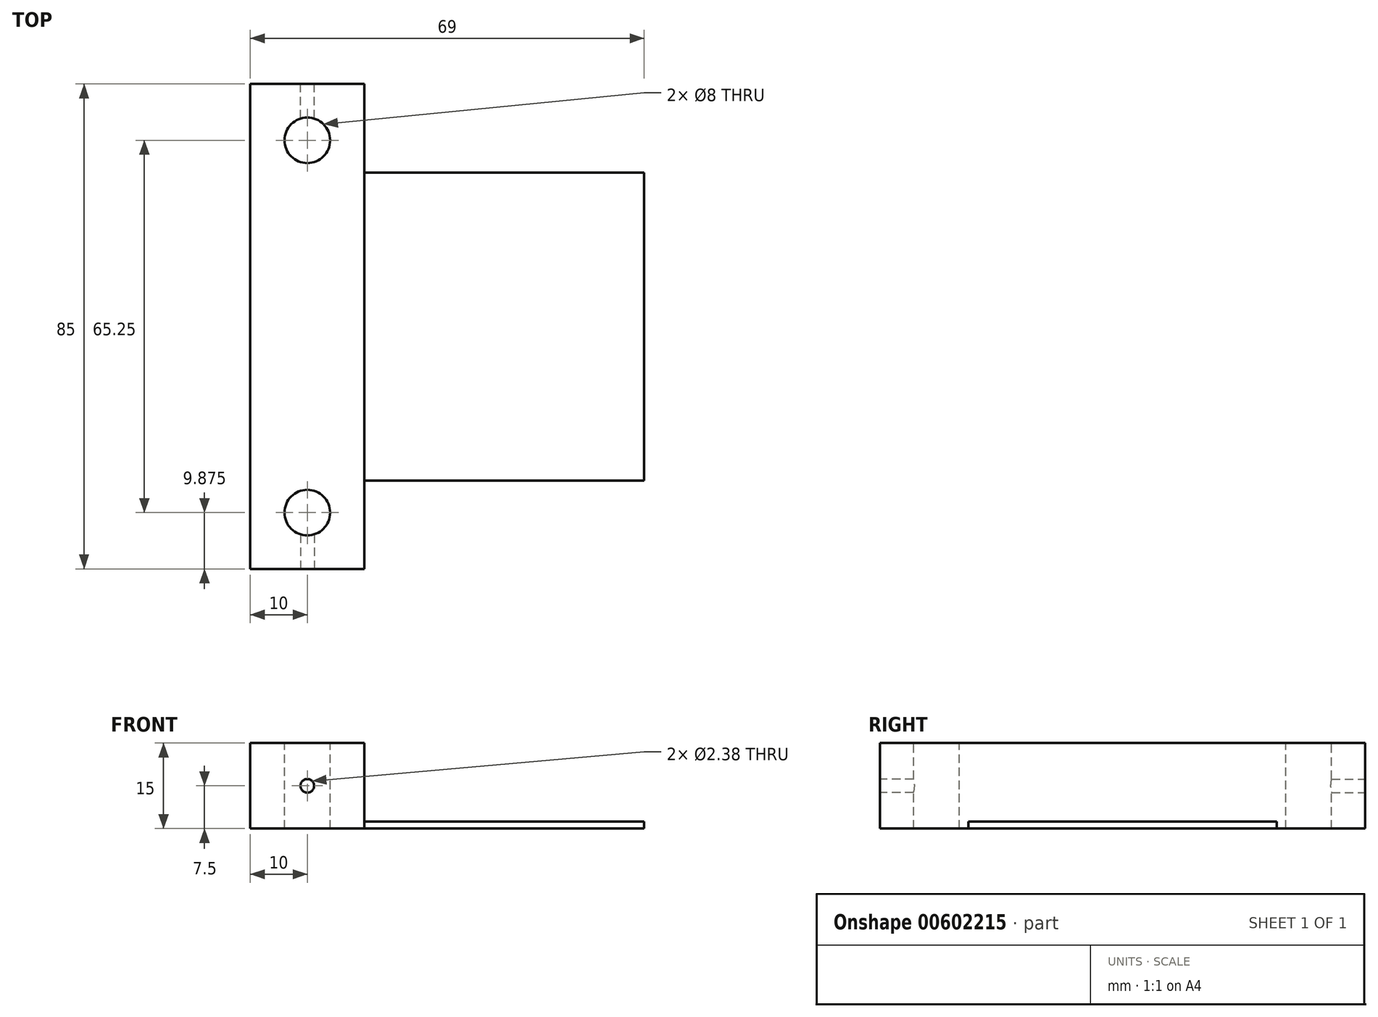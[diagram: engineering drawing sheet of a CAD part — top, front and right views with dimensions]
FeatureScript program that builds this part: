
annotation { "Feature Type Name" : "Feature", "Feature Type Description" : "" }
export const myFeature = defineFeature(function(context is Context, id is Id, definition is map)
    precondition{}
    {
        {
            var Q0;
            Q0=qCreatedBy(makeId("Front.planeOp"),FACE);
            var sketch = newSketch(context, id + "F0", { "sketchPlane" : qUnion([Q0])});
            skLineSegment(sketch, "E0.bottom", {"start": v(0, 0) * mm, "end": v(20, 0) * mm});
            skLineSegment(sketch, "E0.top", {"start": v(0, 15) * mm, "end": v(20, 15) * mm});
            skLineSegment(sketch, "E0.left", {"start": v(0, 0) * mm, "end": v(0, 15) * mm});
            skLineSegment(sketch, "E0.right", {"start": v(20, 0) * mm, "end": v(20, 15) * mm});
            skLineSegment(sketch, "E1", {"start": v(69, 1.2) * mm, "end": v(69, 0) * mm});
            skLineSegment(sketch, "E2", {"start": v(69, 0) * mm, "end": v(20, 0) * mm});
            skLineSegment(sketch, "E3", {"start": v(69, 1.2) * mm, "end": v(20, 1.2) * mm});
            skSolve(sketch);
        }
        {
            var Q0;
            Q0=makeQuery(id+"F0.imprint","IMPRINT",FACE,{"disambiguationData":[TD([[makeQuery(id+"F0.imprint","IMPRINT",EDGE,{"derivedFrom":sQuery(id+"F0.wireOp",EDGE,"E0.right")}),-1.0]])]});
            extrude(context, id + "F1", {"entities" : qUnion([Q0]), "endBound" : BoundingType.SYMMETRIC, "oppositeDirection" : true, "depth" : 53.98 * mm, "offsetDistance" : 25 * mm});
        }
        {
            var Q0;
            Q0=makeQuery(id+"F0.imprint","IMPRINT",FACE,{"disambiguationData":[TD([[makeQuery(id+"F0.imprint","IMPRINT",EDGE,{"derivedFrom":sQuery(id+"F0.wireOp",EDGE,"E0.bottom")}),1.0]])]});
            extrude(context, id + "F2", {"entities" : qUnion([Q0]), "operationType" : NewBodyOperationType.ADD, "endBound" : BoundingType.SYMMETRIC, "depth" : 85 * mm, "offsetDistance" : 25 * mm});
        }
        {
            var Q0;
            Q0=makeQuery(id+"F2.opExtrude","SWEPT_FACE",FACE,{"disambiguationData":[OSD([sQuery(id+"F0.wireOp",EDGE,"E0.top")])]});
            cPlane(context, id + "F3", {"entities" : qUnion([Q0]), "cplaneType" : CPlaneType.OFFSET, "offset" : 0 * mm, "width" : 150 * mm, "height" : 150 * mm});
        }
        {
            var Q0;
            Q0=qCreatedBy(id+"F3.planeOp",FACE);
            var sketch = newSketch(context, id + "F4", { "sketchPlane" : qUnion([Q0])});
            skLineSegment(sketch, "E4.0", {"start": v(0, -42.5) * mm, "end": v(0, 42.5) * mm});
            skLineSegment(sketch, "E4.1", {"start": v(0, -42.5) * mm, "end": v(20, -42.5) * mm});
            skLineSegment(sketch, "E4.2", {"start": v(20, -42.5) * mm, "end": v(20, -42.5) * mm});
            skLineSegment(sketch, "E4.3", {"start": v(20, 42.5) * mm, "end": v(20, 42.5) * mm});
            skLineSegment(sketch, "E4.4", {"start": v(0, 42.5) * mm, "end": v(20, 42.5) * mm});
            skCircle(sketch, "E5", {"center": v(10, -32.62) * mm, "radius": 4 * mm});
            skLineSegment(sketch, "E6", {"start": v(20, -32.62) * mm, "end": v(0, -32.62) * mm, "construction": true});
            skLineSegment(sketch, "E7", {"start": v(20, -36.62) * mm, "end": v(0, -36.62) * mm, "construction": true});
            skCircle(sketch, "E8", {"center": v(10, 32.62) * mm, "radius": 4 * mm});
            skLineSegment(sketch, "E9", {"start": v(20, 32.62) * mm, "end": v(0, 32.62) * mm, "construction": true});
            skLineSegment(sketch, "E10", {"start": v(0, 36.62) * mm, "end": v(20, 36.62) * mm, "construction": true});
            skLineSegment(sketch, "E11", {"start": v(20, -42.5) * mm, "end": v(20, -36.62) * mm, "construction": true});
            skLineSegment(sketch, "E12", {"start": v(20, 36.62) * mm, "end": v(20, 42.5) * mm, "construction": true});
            skSolve(sketch);
        }
        {
            var Q0;
            Q0=makeQuery(id+"F4.imprint","IMPRINT",FACE,{"disambiguationData":[TD([[makeQuery(id+"F4.imprint","IMPRINT",EDGE,{"derivedFrom":sQuery(id+"F4.wireOp",EDGE,"E5")}),1.0]])]});
            var Q1;
            Q1=makeQuery(id+"F4.imprint","IMPRINT",FACE,{"disambiguationData":[TD([[makeQuery(id+"F4.imprint","IMPRINT",EDGE,{"derivedFrom":sQuery(id+"F4.wireOp",EDGE,"E8")}),1.0]])]});
            extrude(context, id + "F5", {"entities" : qUnion([Q0, Q1]), "operationType" : NewBodyOperationType.REMOVE, "oppositeDirection" : true, "depth" : 25 * mm, "offsetDistance" : 25 * mm});
        }
        {
            var Q0;
            Q0=makeQuery(id+"F2.opExtrude","CAP_FACE",FACE,{"disambiguationData":[OSD([sQuery(id+"F0.wireOp",EDGE,"E0.bottom"),sQuery(id+"F0.wireOp",EDGE,"E0.top"),sQuery(id+"F0.wireOp",EDGE,"E0.left"),sQuery(id+"F0.wireOp",EDGE,"E0.right")])],"isStart":false});
            var sketch = newSketch(context, id + "F6", { "sketchPlane" : qUnion([Q0])});
            skCircle(sketch, "E13", {"center": v(10, 7.5) * mm, "radius": 1.19 * mm});
            skPoint(sketch, "E13.centerSnap0", {"position": v(10, 15) * mm});
            skPoint(sketch, "E13.centerSnap1", {"position": v(20, 7.5) * mm});
            skSolve(sketch);
        }
        {
            var Q0;
            Q0=makeQuery(id+"F6.imprint","IMPRINT",FACE,{"disambiguationData":[TD([[makeQuery(id+"F6.imprint","IMPRINT",EDGE,{"derivedFrom":sQuery(id+"F6.wireOp",EDGE,"E13")}),1.0]])]});
            extrude(context, id + "F7", {"entities" : qUnion([Q0]), "operationType" : NewBodyOperationType.REMOVE, "oppositeDirection" : true, "depth" : 8 * mm, "offsetDistance" : 25 * mm});
        }
        {
            var Q0;
            Q0=makeQuery(id+"F2.opExtrude","CAP_FACE",FACE,{"disambiguationData":[OSD([sQuery(id+"F0.wireOp",EDGE,"E0.bottom"),sQuery(id+"F0.wireOp",EDGE,"E0.top"),sQuery(id+"F0.wireOp",EDGE,"E0.left"),sQuery(id+"F0.wireOp",EDGE,"E0.right")])],"isStart":true});
            var sketch = newSketch(context, id + "F8", { "sketchPlane" : qUnion([Q0])});
            skCircle(sketch, "E14", {"center": v(-10, 7.5) * mm, "radius": 1.19 * mm});
            skPoint(sketch, "E14.centerSnap0", {"position": v(0, 7.5) * mm});
            skPoint(sketch, "E14.centerSnap1", {"position": v(-10, 0) * mm});
            skSolve(sketch);
        }
        {
            var Q0;
            Q0=makeQuery(id+"F8.imprint","IMPRINT",FACE,{"disambiguationData":[TD([[makeQuery(id+"F8.imprint","IMPRINT",EDGE,{"derivedFrom":sQuery(id+"F8.wireOp",EDGE,"E14")}),1.0]])]});
            extrude(context, id + "F9", {"entities" : qUnion([Q0]), "operationType" : NewBodyOperationType.REMOVE, "oppositeDirection" : true, "depth" : 8 * mm, "offsetDistance" : 25 * mm});
        }
    });
